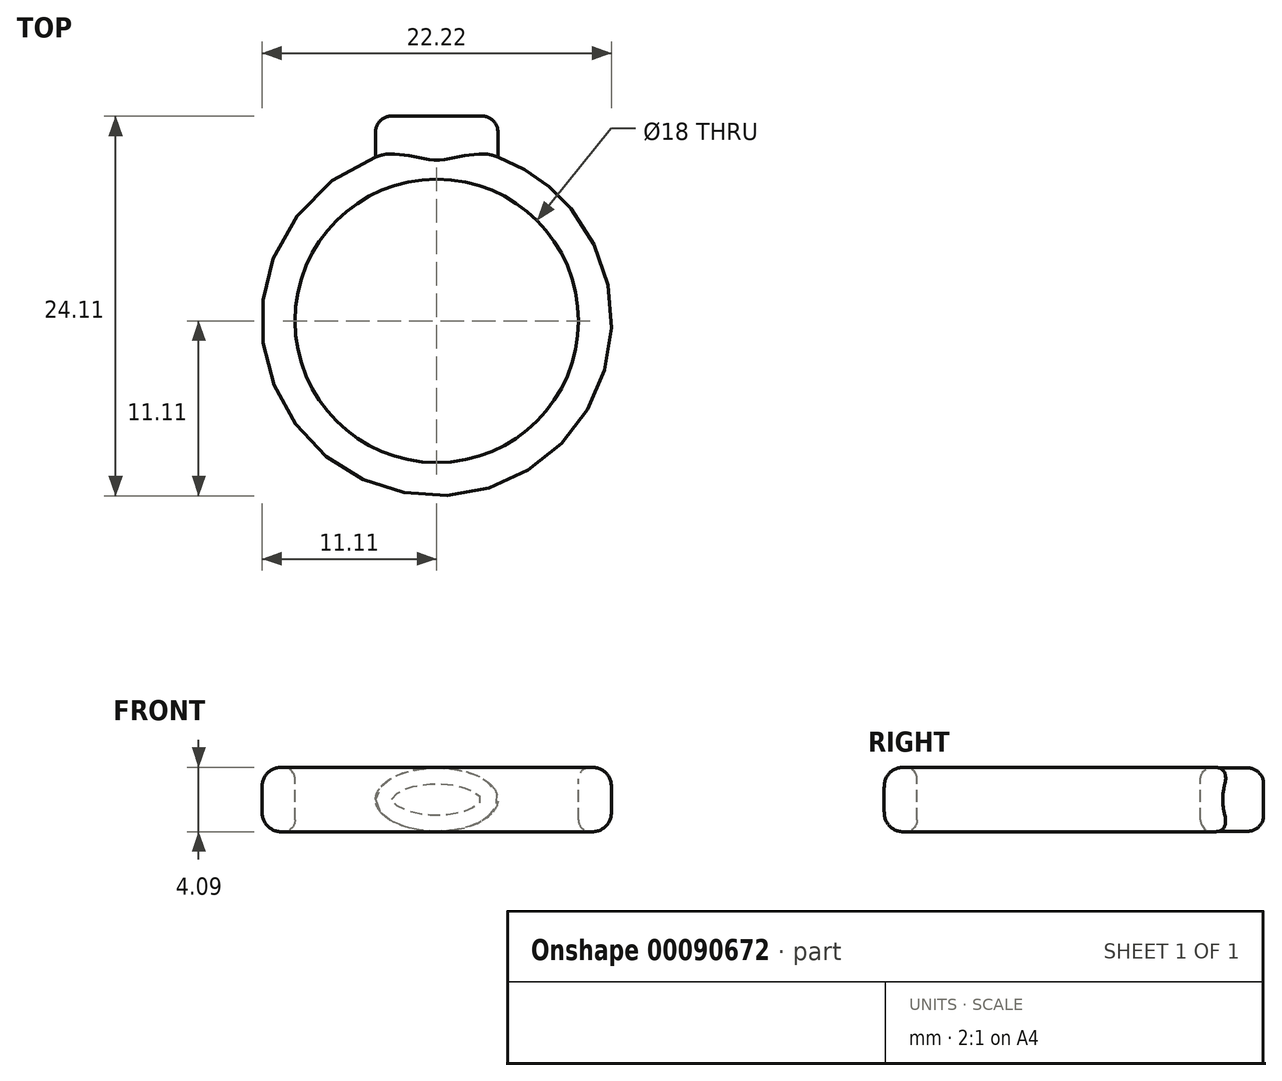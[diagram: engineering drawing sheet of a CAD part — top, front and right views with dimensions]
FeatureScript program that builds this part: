
annotation { "Feature Type Name" : "Feature", "Feature Type Description" : "" }
export const myFeature = defineFeature(function(context is Context, id is Id, definition is map)
    precondition{}
    {
        {
            var Q0;
            Q0=qCreatedBy(makeId("Top.planeOp"),FACE);
            var sketch = newSketch(context, id + "F0", { "sketchPlane" : qUnion([Q0])});
            skCircle(sketch, "E0", {"center": v(0, 0) * mm, "radius": 9 * mm});
            skSolve(sketch);
        }
        {
            var Q0;
            Q0=qSketchRegion(id+"F0",true);
            extrude(context, id + "F1", {"entities" : qUnion([Q0]), "depth" : 5 * mm});
        }
        {
            var Q0;
            Q0=qCreatedBy(makeId("Front.planeOp"),FACE);
            var sketch = newSketch(context, id + "F2", { "sketchPlane" : qUnion([Q0])});
            skLineSegment(sketch, "E1", {"start": v(-9, 0) * mm, "end": v(-9, 4.09) * mm});
            skLineSegment(sketch, "E2", {"start": v(-9, 4.09) * mm, "end": v(-11, 4.09) * mm});
            skLineSegment(sketch, "E3", {"start": v(-9, 0) * mm, "end": v(-11, 0) * mm});
            skEllipticalArc(sketch, "E4", {});
            const initialGuessF2  = {"E4": [-0.009, 0.002044621467089722, 0, 1, 0.006460695860003162, 0.0021083652104055594, 1.248789600770858, 1.8928030528189346]};
            skSetInitialGuess(sketch, initialGuessF2);
            skSolve(sketch);
        }
        {
            var Q0;
            Q0=makeQuery(id+"F2.imprint","IMPRINT",FACE,{"disambiguationData":[TD([[makeQuery(id+"F2.imprint","IMPRINT",EDGE,{"derivedFrom":sQuery(id+"F2.wireOp",EDGE,"E1")}),1.0]])]});
            var Q1;
            Q1=makeQuery(id+"F1.opExtrude","SWEPT_FACE",FACE,{"disambiguationData":[OSD([sQuery(id+"F0.wireOp",EDGE,"E0")])]});
            revolve(context, id + "F3", {"entities" : qUnion([Q0]), "axis" : qUnion([Q1]), "revolveType" : RevolveType.FULL});
        }
        {
            var Q0;
            Q0=makeQuery(id+"F3.opRevolve","SWEPT_EDGE",EDGE,{"disambiguationData":[OSD([sQuery(id+"F2.wireOp",EDGE,"E2"),sQuery(id+"F2.wireOp",EDGE,"E4")])]});
            var Q1;
            Q1=makeQuery(id+"F3.opRevolve","SWEPT_EDGE",EDGE,{"disambiguationData":[OSD([sQuery(id+"F2.wireOp",EDGE,"E3"),sQuery(id+"F2.wireOp",EDGE,"E4")])]});
            fillet(context, id + "F4", {"entities" : qUnion([Q0, Q1]), "radius" : 1.2 * mm, "tangentPropagation" : true, "allowEdgeOverflow" : false});
        }
        {
            var Q0;
            Q0=makeQuery(id+"F3.opRevolve","SWEPT_EDGE",EDGE,{"disambiguationData":[OSD([sQuery(id+"F2.wireOp",EDGE,"E1"),sQuery(id+"F2.wireOp",EDGE,"E3")])]});
            var Q1;
            Q1=makeQuery(id+"F3.opRevolve","SWEPT_EDGE",EDGE,{"disambiguationData":[OSD([sQuery(id+"F2.wireOp",EDGE,"E1"),sQuery(id+"F2.wireOp",EDGE,"E2")])]});
            fillet(context, id + "F5", {"entities" : qUnion([Q0, Q1]), "radius" : .75 * mm, "tangentPropagation" : true, "allowEdgeOverflow" : false});
        }
        {
            var Q0;
            Q0=makeQuery(id+"F1.opExtrude","SWEPT_BODY",BODY,{"disambiguationData":[OSD([sQuery(id+"F0.wireOp",EDGE,"E0")])]});
            deleteBodies(context, id + "F6", {"entities" : qUnion([Q0])});
        }
        {
            var Q0;
            Q0=qCreatedBy(makeId("Front.planeOp"),FACE);
            cPlane(context, id + "F7", {"entities" : qUnion([Q0]), "cplaneType" : CPlaneType.OFFSET, "offset" : 10 * mm, "oppositeDirection" : true, "width" : 150 * mm, "height" : 150 * mm});
        }
        {
            var Q0;
            Q0=qCreatedBy(id+"F7.planeOp",FACE);
            var sketch = newSketch(context, id + "F8", { "sketchPlane" : qUnion([Q0])});
            skEllipse(sketch, "E5", {"center": v(0, 2.04) * mm, "majorRadius": 3.89 * mm, "minorRadius": 2 * mm, "majorAxis": v(-1, 0)});
            skSolve(sketch);
        }
        {
            var Q0;
            Q0 = qSketchRegion(id + "F8", true);
            extrude(context, id + "F9", {"entities" : qUnion([Q0]), "operationType" : NewBodyOperationType.ADD, "oppositeDirection" : true, "depth" : 3 * mm});
        }
        {
            var Q0;
            Q0=makeQuery(id+"F9.opExtrude","CAP_EDGE",EDGE,{"disambiguationData":[OSD([sQuery(id+"F8.wireOp",EDGE,"E5")])],"isStart":false});
            fillet(context, id + "F10", {"entities" : qUnion([Q0]), "radius" : 1 * mm, "tangentPropagation" : true, "allowEdgeOverflow" : false});
        }
    });
